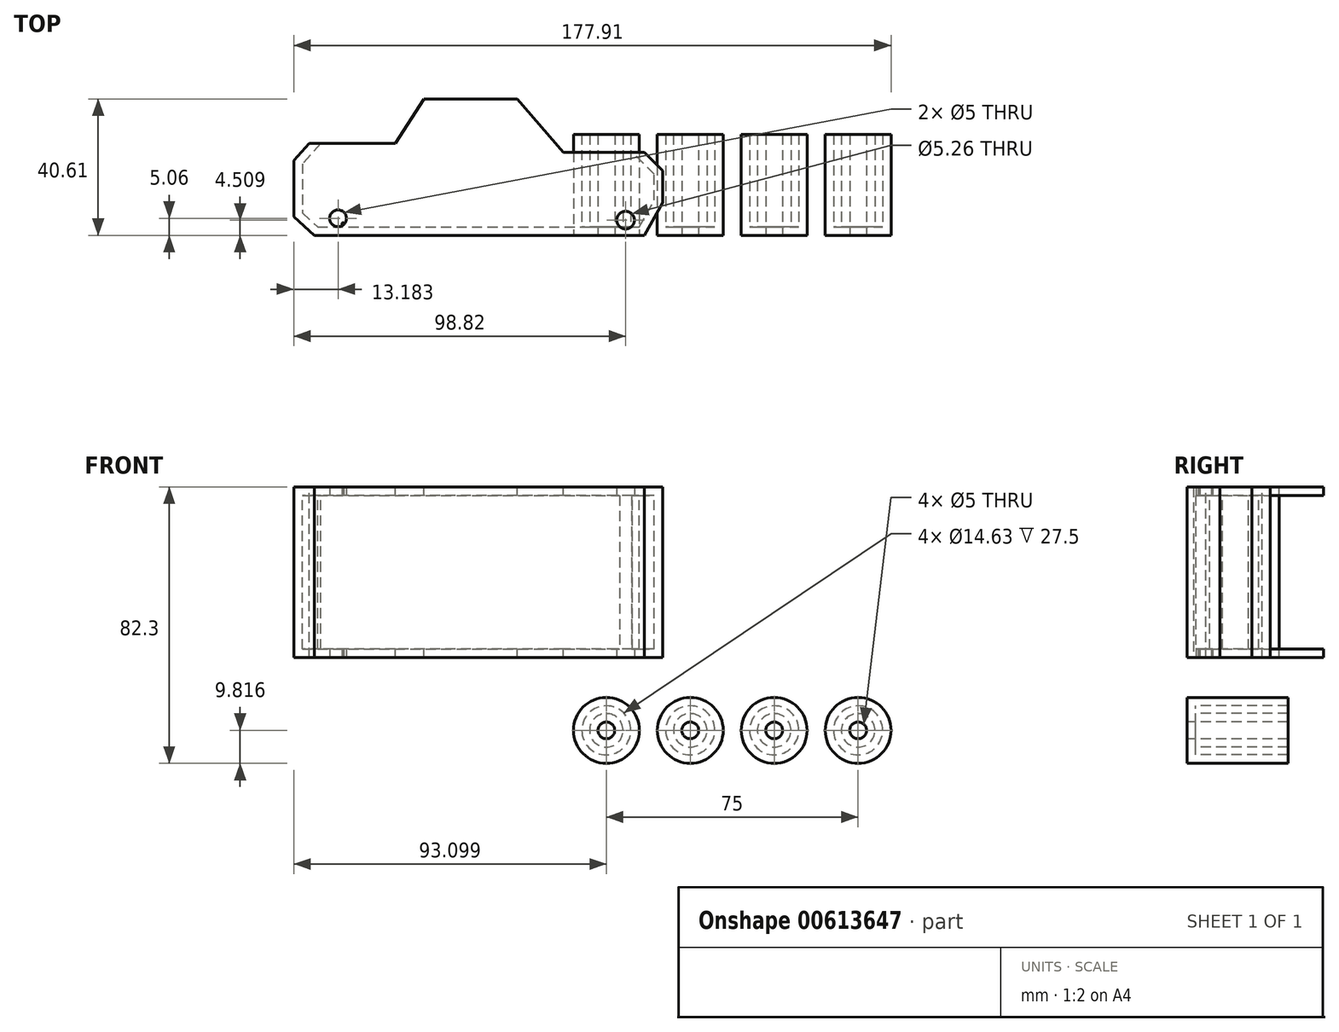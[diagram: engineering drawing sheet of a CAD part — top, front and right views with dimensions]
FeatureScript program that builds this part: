
annotation { "Feature Type Name" : "Feature", "Feature Type Description" : "" }
export const myFeature = defineFeature(function(context is Context, id is Id, definition is map)
    precondition{}
    {
        {
            var Q0;
            Q0=qCreatedBy(makeId("Top.planeOp"),FACE);
            var sketch = newSketch(context, id + "F0", { "sketchPlane" : qUnion([Q0])});
            skLineSegment(sketch, "E0", {"start": v(-38.94, -27.33) * mm, "end": v(59.4, -27.33) * mm});
            skLineSegment(sketch, "E1", {"start": v(59.4, -27.33) * mm, "end": v(64.9, -17.56) * mm});
            skLineSegment(sketch, "E2", {"start": v(64.9, -17.56) * mm, "end": v(64.9, -8.1) * mm});
            skLineSegment(sketch, "E3", {"start": v(64.9, -8.1) * mm, "end": v(59.4, -2.6) * mm});
            skLineSegment(sketch, "E4", {"start": v(59.4, -2.6) * mm, "end": v(35.27, -2.6) * mm});
            skLineSegment(sketch, "E5", {"start": v(35.27, -2.6) * mm, "end": v(21.53, 13.28) * mm});
            skLineSegment(sketch, "E6", {"start": v(21.53, 13.28) * mm, "end": v(-6.26, 13.28) * mm});
            skLineSegment(sketch, "E7", {"start": v(-6.26, 13.28) * mm, "end": v(-14.81, 0) * mm});
            skLineSegment(sketch, "E8", {"start": v(-14.81, 0) * mm, "end": v(-40.46, 0) * mm});
            skLineSegment(sketch, "E9", {"start": v(-40.46, 0) * mm, "end": v(-45.04, -5.04) * mm});
            skLineSegment(sketch, "E10", {"start": v(-45.04, -5.04) * mm, "end": v(-45.04, -14.5) * mm});
            skLineSegment(sketch, "E11", {"start": v(-45.04, -14.5) * mm, "end": v(-45.04, -21.83) * mm});
            skLineSegment(sketch, "E12", {"start": v(-45.04, -21.83) * mm, "end": v(-38.94, -27.33) * mm});
            skCircle(sketch, "E13", {"center": v(53.95, 34.72) * mm, "radius": 12.1 * mm});
            skCircle(sketch, "E14.1.0.0", {"center": v(26.85, 34.72) * mm, "radius": 12.1 * mm});
            skCircle(sketch, "E14.2.0.0", {"center": v(-0.25, 34.72) * mm, "radius": 12.1 * mm});
            skCircle(sketch, "E14.3.0.0", {"center": v(-27.35, 34.72) * mm, "radius": 12.1 * mm});
            skLineSegment(sketch, "E14.direction1", {"start": v(53.95, 34.72) * mm, "end": v(26.85, 34.72) * mm, "construction": true});
            skCircle(sketch, "E15", {"center": v(53.95, 34.72) * mm, "radius": 2.5 * mm});
            skCircle(sketch, "E16", {"center": v(26.85, 34.72) * mm, "radius": 2.5 * mm});
            skCircle(sketch, "E17", {"center": v(-0.25, 34.72) * mm, "radius": 2.5 * mm});
            skCircle(sketch, "E18", {"center": v(-27.35, 34.72) * mm, "radius": 2.5 * mm});
            skSolve(sketch);
        }
        {
            var Q0;
            Q0=makeQuery(id+"F0.imprint","IMPRINT",FACE,{"disambiguationData":[TD([[makeQuery(id+"F0.imprint","IMPRINT",EDGE,{"derivedFrom":sQuery(id+"F0.wireOp",EDGE,"E0")}),1.0]])]});
            extrude(context, id + "F1", {"entities" : qUnion([Q0]), "endBound" : BoundingType.SYMMETRIC, "oppositeDirection" : true, "depth" : 50.8 * mm, "offsetDistance" : 25.4 * mm});
        }
        {
            var Q0;
            Q0=makeQuery(id+"F1.opExtrude","SWEPT_FACE",FACE,{"disambiguationData":[OSD([sQuery(id+"F0.wireOp",EDGE,"E6")])]});
            var Q1;
            Q1=makeQuery(id+"F1.opExtrude","SWEPT_FACE",FACE,{"disambiguationData":[OSD([sQuery(id+"F0.wireOp",EDGE,"E7")])]});
            var Q2;
            Q2=makeQuery(id+"F1.opExtrude","SWEPT_FACE",FACE,{"disambiguationData":[OSD([sQuery(id+"F0.wireOp",EDGE,"E8")])]});
            var Q3;
            Q3=makeQuery(id+"F1.opExtrude","SWEPT_FACE",FACE,{"disambiguationData":[OSD([sQuery(id+"F0.wireOp",EDGE,"E5")])]});
            var Q4;
            Q4=makeQuery(id+"F1.opExtrude","SWEPT_FACE",FACE,{"disambiguationData":[OSD([sQuery(id+"F0.wireOp",EDGE,"E4")])]});
            shell(context, id + "F2", {"entities" : qUnion([Q0, Q1, Q2, Q3, Q4]), "thickness" : 2.54 * mm});
        }
        {
            var Q0;
            Q0=makeQuery(id+"F1.opExtrude","CAP_FACE",FACE,{"disambiguationData":[OSD([sQuery(id+"F0.wireOp",EDGE,"E0"),sQuery(id+"F0.wireOp",EDGE,"E1"),sQuery(id+"F0.wireOp",EDGE,"E2"),sQuery(id+"F0.wireOp",EDGE,"E3"),sQuery(id+"F0.wireOp",EDGE,"E4"),sQuery(id+"F0.wireOp",EDGE,"E5"),sQuery(id+"F0.wireOp",EDGE,"E6"),sQuery(id+"F0.wireOp",EDGE,"E7"),sQuery(id+"F0.wireOp",EDGE,"E8"),sQuery(id+"F0.wireOp",EDGE,"E9"),sQuery(id+"F0.wireOp",EDGE,"E10"),sQuery(id+"F0.wireOp",EDGE,"E11"),sQuery(id+"F0.wireOp",EDGE,"E12")])],"isStart":false});
            var sketch = newSketch(context, id + "F3", { "sketchPlane" : qUnion([Q0])});
            skCircle(sketch, "E19", {"center": v(-30.45, 23.84) * mm, "radius": 0.25 * mm});
            skCircle(sketch, "E20", {"center": v(53.78, 22.82) * mm, "radius": 2.63 * mm});
            skCircle(sketch, "E21", {"center": v(-31.86, 22.27) * mm, "radius": 2.5 * mm});
            skSolve(sketch);
        }
        {
            var Q0;
            Q0=makeQuery(id+"F3.imprint","IMPRINT",FACE,{"disambiguationData":[TD([[makeQuery(id+"F3.imprint","IMPRINT",EDGE,{"derivedFrom":sQuery(id+"F3.wireOp",EDGE,"E20")}),1.0]])]});
            var Q1;
            Q1=makeQuery(id+"F3.imprint","IMPRINT",FACE,{"disambiguationData":[TD([[makeQuery(id+"F3.imprint","IMPRINT",EDGE,{"derivedFrom":sQuery(id+"F3.wireOp",EDGE,"E19")}),-1.0]])]});
            extrude(context, id + "F4", {"entities" : qUnion([Q0, Q1]), "operationType" : NewBodyOperationType.REMOVE, "oppositeDirection" : true, "depth" : 80 * mm, "offsetDistance" : 25 * mm});
        }
        {
            var Q0;
            Q0=makeQuery(id+"F1.opExtrude","SWEPT_FACE",FACE,{"disambiguationData":[OSD([sQuery(id+"F0.wireOp",EDGE,"E0")])]});
            var sketch = newSketch(context, id + "F5", { "sketchPlane" : qUnion([Q0])});
            skCircle(sketch, "E22", {"center": v(48.06, -47.08) * mm, "radius": 9.81 * mm});
            skCircle(sketch, "E23", {"center": v(48.06, -47.08) * mm, "radius": 2.5 * mm});
            skCircle(sketch, "E24.1.0.0", {"center": v(73.06, -47.08) * mm, "radius": 9.81 * mm});
            skCircle(sketch, "E24.1.0.1", {"center": v(73.06, -47.08) * mm, "radius": 2.5 * mm});
            skCircle(sketch, "E24.2.0.0", {"center": v(98.06, -47.08) * mm, "radius": 9.81 * mm});
            skCircle(sketch, "E24.2.0.1", {"center": v(98.06, -47.08) * mm, "radius": 2.5 * mm});
            skLineSegment(sketch, "E24.direction1", {"start": v(48.06, -47.08) * mm, "end": v(73.06, -47.08) * mm, "construction": true});
            skCircle(sketch, "E25.0.3.0", {"center": v(123.06, -47.08) * mm, "radius": 9.81 * mm});
            skCircle(sketch, "E25.2.3.0", {"center": v(123.06, -47.08) * mm, "radius": 2.5 * mm});
            skSolve(sketch);
        }
        {
            var Q0;
            Q0=makeQuery(id+"F5.imprint","IMPRINT",FACE,{"disambiguationData":[TD([[makeQuery(id+"F5.imprint","IMPRINT",EDGE,{"derivedFrom":sQuery(id+"F5.wireOp",EDGE,"E25.0.3.0")}),1.0]])]});
            var Q1;
            Q1=makeQuery(id+"F5.imprint","IMPRINT",FACE,{"disambiguationData":[TD([[makeQuery(id+"F5.imprint","IMPRINT",EDGE,{"derivedFrom":sQuery(id+"F5.wireOp",EDGE,"E24.2.0.0")}),1.0]])]});
            var Q2;
            Q2=makeQuery(id+"F5.imprint","IMPRINT",FACE,{"disambiguationData":[TD([[makeQuery(id+"F5.imprint","IMPRINT",EDGE,{"derivedFrom":sQuery(id+"F5.wireOp",EDGE,"E24.1.0.0")}),1.0]])]});
            var Q3;
            Q3=makeQuery(id+"F5.imprint","IMPRINT",FACE,{"disambiguationData":[TD([[makeQuery(id+"F5.imprint","IMPRINT",EDGE,{"derivedFrom":sQuery(id+"F5.wireOp",EDGE,"E22")}),1.0]])]});
            extrude(context, id + "F6", {"entities" : qUnion([Q0, Q1, Q2, Q3]), "oppositeDirection" : true, "depth" : 30 * mm, "offsetDistance" : 25 * mm});
        }
        {
            var Q0;
            Q0=makeQuery(id+"F6.opExtrude","CAP_FACE",FACE,{"disambiguationData":[OSD([sQuery(id+"F5.wireOp",EDGE,"E25.0.3.0"),sQuery(id+"F5.wireOp",EDGE,"E25.2.3.0")])],"isStart":false});
            var Q1;
            Q1=makeQuery(id+"F6.opExtrude","CAP_FACE",FACE,{"disambiguationData":[OSD([sQuery(id+"F5.wireOp",EDGE,"E24.2.0.0"),sQuery(id+"F5.wireOp",EDGE,"E24.2.0.1")])],"isStart":false});
            var Q2;
            Q2=makeQuery(id+"F6.opExtrude","CAP_FACE",FACE,{"disambiguationData":[OSD([sQuery(id+"F5.wireOp",EDGE,"E24.1.0.0"),sQuery(id+"F5.wireOp",EDGE,"E24.1.0.1")])],"isStart":false});
            var Q3;
            Q3=makeQuery(id+"F6.opExtrude","CAP_FACE",FACE,{"disambiguationData":[OSD([sQuery(id+"F5.wireOp",EDGE,"E22"),sQuery(id+"F5.wireOp",EDGE,"E23")])],"isStart":false});
            shell(context, id + "F7", {"entities" : qUnion([Q0, Q1, Q2, Q3]), "thickness" : 2.5 * mm});
        }
    });
